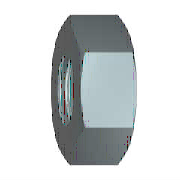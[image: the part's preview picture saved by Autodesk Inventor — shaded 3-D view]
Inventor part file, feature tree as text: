
AUTODESK INVENTOR PART (.ipt)
format: ipt  version: 2025.1 (Build 291241020, 241B)  size: 164,864 bytes
history: native  units: mm (DEFAULTED — no unit token found)
features: chamfer x1, hole x1, other x1, plane x1
ambient origin geometry x7: Origin, YZ Plane, XZ Plane, X Axis, Y Axis, Z Axis, Center Point
bodies: Solid1 (feature_tree), Body (feature_tree)
feature tree (4):
  chamfer  "Chamfer1"  Distance=24.248711mm
  hole  "Thread"  [1 undecoded]
  other  "Work Axis1"
  plane  "Work Plane1"
note: 1 required parameter value undecoded (feature->parameter linkage not recoverable at this tier; creation-order binding heuristic only, values carry confidence <= 0.55)
